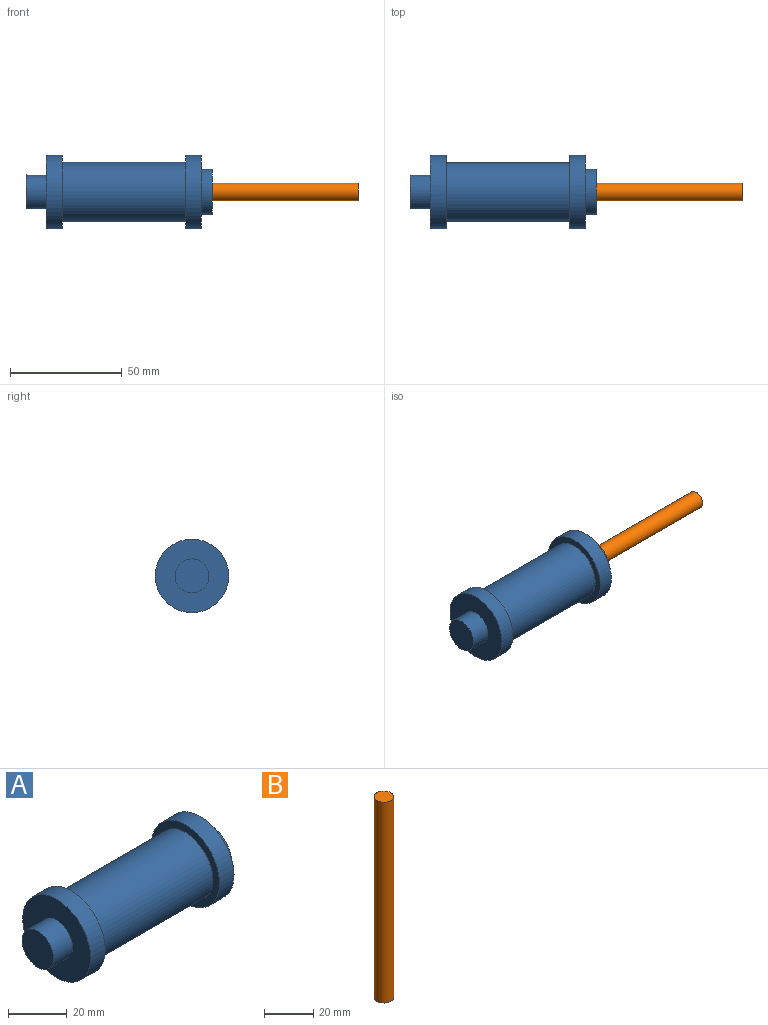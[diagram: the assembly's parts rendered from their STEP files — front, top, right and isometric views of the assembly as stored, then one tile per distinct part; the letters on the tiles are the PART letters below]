
ASSEMBLY  parts=2 mates=1
PART A: 13 faces, bbox 83.4x32.8x32.8 mm
  f0: plane 15.2x15.2mm, normal (-1,0,0), area 181.5mm2, adj f10
  f1: plane 20.4x20.4mm, normal (1,0,0), area 276.7mm2, adj f2,f11
  f2: cylinder r=10.2mm len=20.4mm, axis (1,0,0), area 320.5mm2, adj f1,f3
  f3: plane 32.8x32.8mm, normal (1,0,0), area 518.2mm2, adj f2,f4
  f4: cylinder r=16.4mm len=32.8mm, axis (1,0,0), area 721.4mm2, adj f3,f5
  f5: plane 32.8x32.8mm, normal (-1,0,0), area 297.6mm2, adj f4,f6
  f6: cylinder r=13.2mm len=55.2mm, axis (1,0,0), area 4578.6mm2, adj f5,f7
  f7: plane 32.8x32.8mm, normal (1,0,0), area 297.6mm2, adj f6,f8
  f8: cylinder r=16.4mm len=32.8mm, axis (1,0,0), area 721.4mm2, adj f7,f9
  f9: plane 32.8x32.8mm, normal (-1,0,0), area 663.6mm2, adj f8,f10
  f10: cylinder r=7.6mm len=15.2mm, axis (1,0,0), area 437.2mm2, adj f0,f9
  f11: cylinder r=4mm len=60mm, axis (1,0,0), area 1508mm2, adj f1,f12
  f12: plane 8x8mm, normal (1,0,0), area 50.3mm2, adj f11
PART B: 3 faces, bbox 8x8x100 mm
  f0: cylinder r=4mm len=100mm, axis (0,0,-1), area 2513.3mm2, adj f1,f2
  f1: plane 8x8mm, normal (0,0,1), area 50.3mm2, adj f0
  f2: plane 8x8mm, normal (0,0,-1), area 50.3mm2, adj f0
PLACE A t=(-5.74,4.15,11.19)mm fixed
PLACE B rot(axis=(0,-1,0),90deg) t=(142.65,4.15,11.19)mm
MATE slider B.f0 <-> A.f2  axis (1,0,0) through (42.65,4.15,11.19)mm
